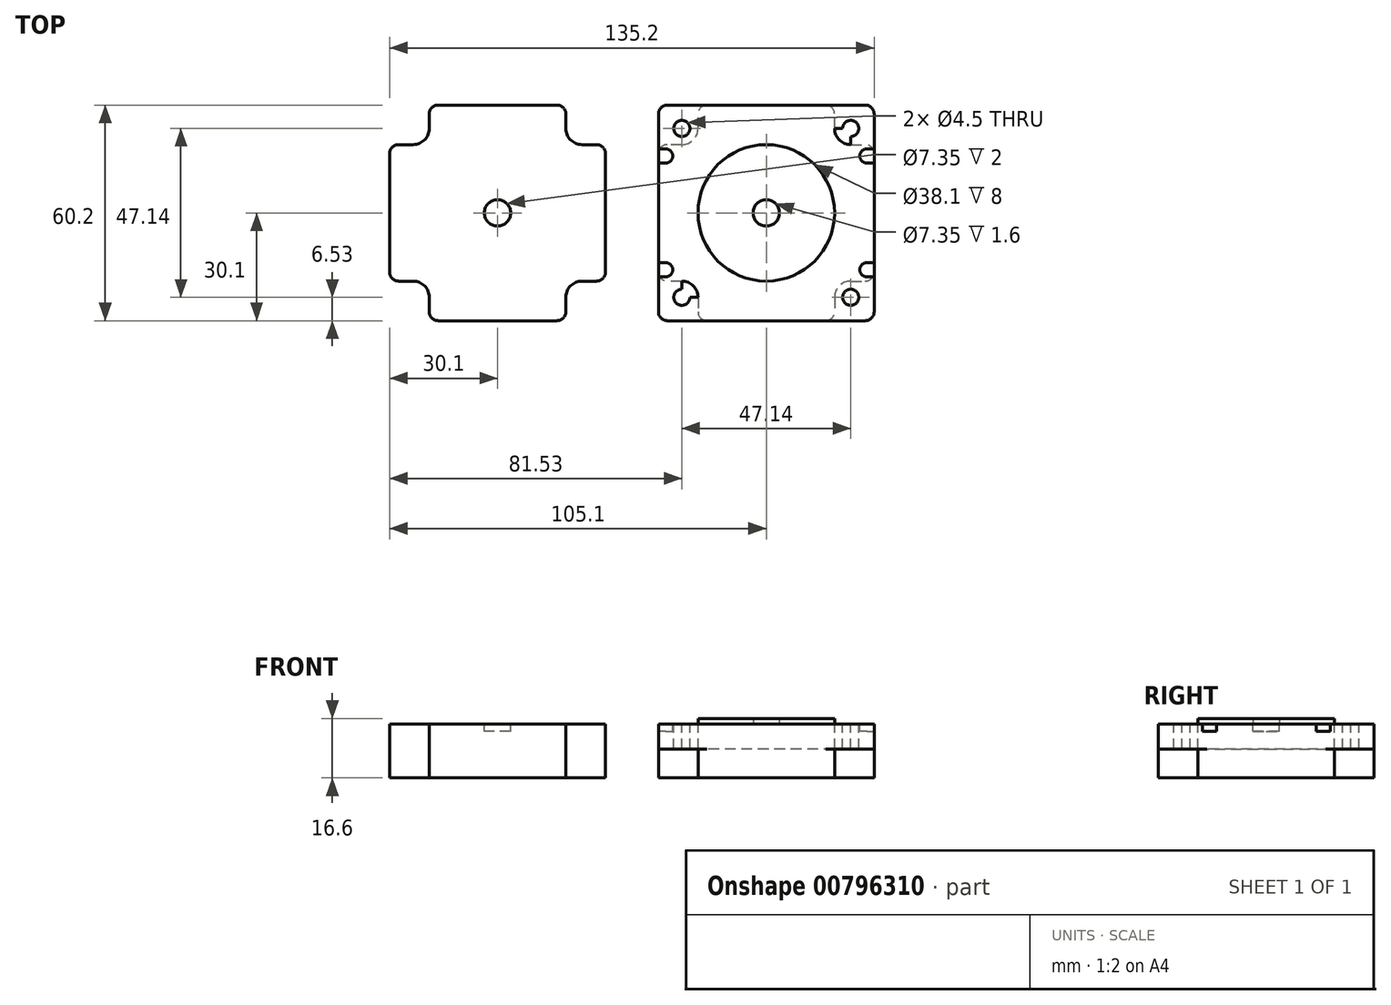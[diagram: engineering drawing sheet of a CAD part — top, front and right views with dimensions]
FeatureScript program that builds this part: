
annotation { "Feature Type Name" : "Feature", "Feature Type Description" : "" }
export const myFeature = defineFeature(function(context is Context, id is Id, definition is map)
    precondition{}
    {
        {
            var Q0;
            Q0=qCreatedBy(makeId("Top.planeOp"),FACE);
            var sketch = newSketch(context, id + "F0", { "sketchPlane" : qUnion([Q0])});
            skLineSegment(sketch, "E0.bottom", {"start": v(30.1, 30.1) * mm, "end": v(-30.1, 30.1) * mm});
            skLineSegment(sketch, "E0.top", {"start": v(30.1, -30.1) * mm, "end": v(-30.1, -30.1) * mm});
            skLineSegment(sketch, "E0.left", {"start": v(30.1, 30.1) * mm, "end": v(30.1, -30.1) * mm});
            skLineSegment(sketch, "E0.right", {"start": v(-30.1, 30.1) * mm, "end": v(-30.1, -30.1) * mm});
            skPoint(sketch, "E0.middle", {"position": v(0, 0) * mm});
            skLineSegment(sketch, "E1", {"start": v(-30.1, 30.1) * mm, "end": v(30.1, -30.1) * mm, "construction": true});
            skLineSegment(sketch, "E2", {"start": v(30.1, 30.1) * mm, "end": v(-30.1, -30.1) * mm, "construction": true});
            skLineSegment(sketch, "E3", {"start": v(-23.57, 23.57) * mm, "end": v(23.57, 23.57) * mm});
            skLineSegment(sketch, "E4", {"start": v(23.57, 23.57) * mm, "end": v(23.57, -23.57) * mm});
            skLineSegment(sketch, "E5", {"start": v(23.57, -23.57) * mm, "end": v(-23.57, -23.57) * mm});
            skLineSegment(sketch, "E6", {"start": v(-23.57, -23.57) * mm, "end": v(-23.57, 23.57) * mm});
            skCircle(sketch, "E7", {"center": v(0, 0) * mm, "radius": 19.05 * mm});
            skCircle(sketch, "E8", {"center": v(-23.57, 23.57) * mm, "radius": 2.25 * mm});
            skCircle(sketch, "E9", {"center": v(23.57, 23.57) * mm, "radius": 2.25 * mm});
            skCircle(sketch, "E10", {"center": v(23.57, -23.57) * mm, "radius": 2.25 * mm});
            skCircle(sketch, "E11", {"center": v(-23.57, -23.57) * mm, "radius": 2.25 * mm});
            skCircle(sketch, "E12", {"center": v(0, 0) * mm, "radius": 3.67 * mm});
            skLineSegment(sketch, "E13", {"start": v(0, 0) * mm, "end": v(0, -23.57) * mm, "construction": true});
            skArc(sketch, "E14", {"start": v(-28.1, -17.88) * mm, "mid": v(-26.1, -15.88) * mm, "end": v(-28.1, -13.88) * mm});
            skLineSegment(sketch, "E15", {"start": v(0, 0) * mm, "end": v(-23.57, 0) * mm, "construction": true});
            skLineSegment(sketch, "E16", {"start": v(-28.1, -13.88) * mm, "end": v(-30.1, -13.88) * mm});
            skLineSegment(sketch, "E17", {"start": v(-28.1, -17.88) * mm, "end": v(-30.1, -17.88) * mm});
            skArc(sketch, "E18", {"start": v(-28.1, -13.88) * mm, "mid": v(-30.1, -15.88) * mm, "end": v(-28.1, -17.88) * mm, "construction": true});
            skLineSegment(sketch, "E19.MirrorCS", {"start": v(-28.1, 13.88) * mm, "end": v(-30.1, 13.88) * mm});
            skArc(sketch, "E20.MirrorCS", {"start": v(-28.1, 17.88) * mm, "mid": v(-26.1, 15.88) * mm, "end": v(-28.1, 13.88) * mm});
            skLineSegment(sketch, "E21.MirrorCS", {"start": v(-28.1, 17.88) * mm, "end": v(-30.1, 17.88) * mm});
            skLineSegment(sketch, "E22.MirrorCS", {"start": v(28.1, -13.87) * mm, "end": v(30.1, -13.87) * mm});
            skArc(sketch, "E23.MirrorCS", {"start": v(28.1, -17.88) * mm, "mid": v(26.1, -15.88) * mm, "end": v(28.1, -13.88) * mm});
            skLineSegment(sketch, "E24.MirrorCS", {"start": v(28.1, -17.88) * mm, "end": v(30.1, -17.88) * mm});
            skLineSegment(sketch, "E25.MirrorCS", {"start": v(28.1, 13.88) * mm, "end": v(30.1, 13.88) * mm});
            skArc(sketch, "E26.MirrorCS", {"start": v(28.1, 17.88) * mm, "mid": v(26.1, 15.88) * mm, "end": v(28.1, 13.88) * mm});
            skLineSegment(sketch, "E27.MirrorCS", {"start": v(28.1, 17.88) * mm, "end": v(30.1, 17.88) * mm});
            skLineSegment(sketch, "E28", {"start": v(-23.57, 19.05) * mm, "end": v(-30.1, 19.05) * mm});
            skLineSegment(sketch, "E29.MirrorCS", {"start": v(-23.57, -19.05) * mm, "end": v(-30.1, -19.05) * mm});
            skLineSegment(sketch, "E30", {"start": v(-19.05, -23.57) * mm, "end": v(-19.05, -30.1) * mm});
            skLineSegment(sketch, "E31.MirrorCS", {"start": v(19.05, -23.57) * mm, "end": v(19.05, -30.1) * mm});
            skArc(sketch, "E32", {"start": v(-23.57, -19.05) * mm, "mid": v(-20.37, -20.37) * mm, "end": v(-19.05, -23.57) * mm});
            skArc(sketch, "E33.MirrorCS", {"start": v(-23.57, 19.05) * mm, "mid": v(-20.37, 20.37) * mm, "end": v(-19.05, 23.57) * mm});
            skLineSegment(sketch, "E34.MirrorCS", {"start": v(-19.05, 23.57) * mm, "end": v(-19.05, 30.1) * mm});
            skArc(sketch, "E35.MirrorCS", {"start": v(23.57, -19.05) * mm, "mid": v(20.37, -20.37) * mm, "end": v(19.05, -23.57) * mm});
            skLineSegment(sketch, "E36.MirrorCS", {"start": v(23.57, -19.05) * mm, "end": v(30.1, -19.05) * mm});
            skLineSegment(sketch, "E37.MirrorCS", {"start": v(23.57, 19.05) * mm, "end": v(30.1, 19.05) * mm});
            skArc(sketch, "E38.MirrorCS", {"start": v(23.57, 19.05) * mm, "mid": v(20.37, 20.37) * mm, "end": v(19.05, 23.57) * mm});
            skLineSegment(sketch, "E39.MirrorCS", {"start": v(19.05, 23.57) * mm, "end": v(19.05, 30.1) * mm});
            skLineSegment(sketch, "E40.1.0.0", {"start": v(-75, 0) * mm, "end": v(-75, -23.57) * mm, "construction": true});
            skLineSegment(sketch, "E40.1.0.1", {"start": v(-55.95, -23.57) * mm, "end": v(-55.95, -30.1) * mm});
            skArc(sketch, "E40.1.0.2", {"start": v(-51.43, -19.05) * mm, "mid": v(-54.63, -20.37) * mm, "end": v(-55.95, -23.57) * mm});
            skLineSegment(sketch, "E40.1.0.3", {"start": v(-51.43, -19.05) * mm, "end": v(-44.9, -19.05) * mm});
            skLineSegment(sketch, "E40.1.0.4", {"start": v(-44.9, 30.1) * mm, "end": v(-44.9, -30.1) * mm});
            skLineSegment(sketch, "E40.1.0.5", {"start": v(-51.43, 19.05) * mm, "end": v(-44.9, 19.05) * mm});
            skArc(sketch, "E40.1.0.6", {"start": v(-51.43, 19.05) * mm, "mid": v(-54.63, 20.37) * mm, "end": v(-55.95, 23.57) * mm});
            skLineSegment(sketch, "E40.1.0.7", {"start": v(-55.95, 23.57) * mm, "end": v(-55.95, 30.1) * mm});
            skLineSegment(sketch, "E40.1.0.8", {"start": v(-44.9, 30.1) * mm, "end": v(-105.1, 30.1) * mm});
            skLineSegment(sketch, "E40.1.0.9", {"start": v(-94.05, 23.57) * mm, "end": v(-94.05, 30.1) * mm});
            skArc(sketch, "E40.1.0.10", {"start": v(-98.57, 19.05) * mm, "mid": v(-95.37, 20.37) * mm, "end": v(-94.05, 23.57) * mm});
            skLineSegment(sketch, "E40.1.0.11", {"start": v(-98.57, 19.05) * mm, "end": v(-105.1, 19.05) * mm});
            skLineSegment(sketch, "E40.1.0.12", {"start": v(-105.1, 30.1) * mm, "end": v(-105.1, -30.1) * mm});
            skLineSegment(sketch, "E40.1.0.13", {"start": v(-98.57, -19.05) * mm, "end": v(-105.1, -19.05) * mm});
            skArc(sketch, "E40.1.0.14", {"start": v(-98.57, -19.05) * mm, "mid": v(-95.37, -20.37) * mm, "end": v(-94.05, -23.57) * mm});
            skLineSegment(sketch, "E40.1.0.15", {"start": v(-94.05, -23.57) * mm, "end": v(-94.05, -30.1) * mm});
            skLineSegment(sketch, "E40.1.0.16", {"start": v(-44.9, -30.1) * mm, "end": v(-105.1, -30.1) * mm});
            skCircle(sketch, "E40.1.0.17", {"center": v(-75, 0) * mm, "radius": 3.67 * mm});
            skLineSegment(sketch, "E40.2.0.0", {"start": v(-150, 0) * mm, "end": v(-150, -23.57) * mm, "construction": true});
            skLineSegment(sketch, "E40.2.0.1", {"start": v(-130.95, -23.57) * mm, "end": v(-130.95, -30.1) * mm});
            skArc(sketch, "E40.2.0.2", {"start": v(-126.43, -19.05) * mm, "mid": v(-129.63, -20.37) * mm, "end": v(-130.95, -23.57) * mm});
            skLineSegment(sketch, "E40.2.0.3", {"start": v(-126.43, -19.05) * mm, "end": v(-119.9, -19.05) * mm});
            skLineSegment(sketch, "E40.2.0.4", {"start": v(-119.9, 30.1) * mm, "end": v(-119.9, -30.1) * mm});
            skLineSegment(sketch, "E40.2.0.5", {"start": v(-126.43, 19.05) * mm, "end": v(-119.9, 19.05) * mm});
            skArc(sketch, "E40.2.0.6", {"start": v(-126.43, 19.05) * mm, "mid": v(-129.63, 20.37) * mm, "end": v(-130.95, 23.57) * mm});
            skLineSegment(sketch, "E40.2.0.7", {"start": v(-130.95, 23.57) * mm, "end": v(-130.95, 30.1) * mm});
            skLineSegment(sketch, "E40.2.0.8", {"start": v(-119.9, 30.1) * mm, "end": v(-180.1, 30.1) * mm});
            skLineSegment(sketch, "E40.2.0.9", {"start": v(-169.05, 23.57) * mm, "end": v(-169.05, 30.1) * mm});
            skArc(sketch, "E40.2.0.10", {"start": v(-173.57, 19.05) * mm, "mid": v(-170.37, 20.37) * mm, "end": v(-169.05, 23.57) * mm});
            skLineSegment(sketch, "E40.2.0.11", {"start": v(-173.57, 19.05) * mm, "end": v(-180.1, 19.05) * mm});
            skLineSegment(sketch, "E40.2.0.12", {"start": v(-180.1, 30.1) * mm, "end": v(-180.1, -30.1) * mm});
            skLineSegment(sketch, "E40.2.0.13", {"start": v(-173.57, -19.05) * mm, "end": v(-180.1, -19.05) * mm});
            skArc(sketch, "E40.2.0.14", {"start": v(-173.57, -19.05) * mm, "mid": v(-170.37, -20.37) * mm, "end": v(-169.05, -23.57) * mm});
            skLineSegment(sketch, "E40.2.0.15", {"start": v(-169.05, -23.57) * mm, "end": v(-169.05, -30.1) * mm});
            skLineSegment(sketch, "E40.2.0.16", {"start": v(-119.9, -30.1) * mm, "end": v(-180.1, -30.1) * mm});
            skCircle(sketch, "E40.2.0.17", {"center": v(-150, 0) * mm, "radius": 3.67 * mm});
            skLineSegment(sketch, "E40.direction1", {"start": v(0, -23.57) * mm, "end": v(-75, -23.57) * mm, "construction": true});
            skLineSegment(sketch, "E41.0.3.0", {"start": v(-225, 0) * mm, "end": v(-225, -23.57) * mm, "construction": true});
            skLineSegment(sketch, "E41.3.3.0", {"start": v(-205.95, -23.57) * mm, "end": v(-205.95, -30.1) * mm});
            skArc(sketch, "E41.6.3.0", {"start": v(-201.43, -19.05) * mm, "mid": v(-204.63, -20.37) * mm, "end": v(-205.95, -23.57) * mm});
            skLineSegment(sketch, "E41.10.3.0", {"start": v(-201.43, -19.05) * mm, "end": v(-194.9, -19.05) * mm});
            skLineSegment(sketch, "E41.13.3.0", {"start": v(-194.9, 30.1) * mm, "end": v(-194.9, -30.1) * mm});
            skLineSegment(sketch, "E41.16.3.0", {"start": v(-201.43, 19.05) * mm, "end": v(-194.9, 19.05) * mm});
            skArc(sketch, "E41.19.3.0", {"start": v(-201.43, 19.05) * mm, "mid": v(-204.63, 20.37) * mm, "end": v(-205.95, 23.57) * mm});
            skLineSegment(sketch, "E41.23.3.0", {"start": v(-205.95, 23.57) * mm, "end": v(-205.95, 30.1) * mm});
            skLineSegment(sketch, "E41.26.3.0", {"start": v(-194.9, 30.1) * mm, "end": v(-255.1, 30.1) * mm});
            skLineSegment(sketch, "E41.29.3.0", {"start": v(-244.05, 23.57) * mm, "end": v(-244.05, 30.1) * mm});
            skArc(sketch, "E41.32.3.0", {"start": v(-248.57, 19.05) * mm, "mid": v(-245.37, 20.37) * mm, "end": v(-244.05, 23.57) * mm});
            skLineSegment(sketch, "E41.36.3.0", {"start": v(-248.57, 19.05) * mm, "end": v(-255.1, 19.05) * mm});
            skLineSegment(sketch, "E41.39.3.0", {"start": v(-255.1, 30.1) * mm, "end": v(-255.1, -30.1) * mm});
            skLineSegment(sketch, "E41.42.3.0", {"start": v(-248.57, -19.05) * mm, "end": v(-255.1, -19.05) * mm});
            skArc(sketch, "E41.45.3.0", {"start": v(-248.57, -19.05) * mm, "mid": v(-245.37, -20.37) * mm, "end": v(-244.05, -23.57) * mm});
            skLineSegment(sketch, "E41.49.3.0", {"start": v(-244.05, -23.57) * mm, "end": v(-244.05, -30.1) * mm});
            skLineSegment(sketch, "E41.52.3.0", {"start": v(-194.9, -30.1) * mm, "end": v(-255.1, -30.1) * mm});
            skCircle(sketch, "E41.55.3.0", {"center": v(-225, 0) * mm, "radius": 3.67 * mm});
            skLineSegment(sketch, "E41.0.4.0", {"start": v(-300, 0) * mm, "end": v(-300, -23.57) * mm, "construction": true});
            skLineSegment(sketch, "E41.3.4.0", {"start": v(-280.95, -23.57) * mm, "end": v(-280.95, -30.1) * mm});
            skArc(sketch, "E41.6.4.0", {"start": v(-276.43, -19.05) * mm, "mid": v(-279.63, -20.37) * mm, "end": v(-280.95, -23.57) * mm});
            skLineSegment(sketch, "E41.10.4.0", {"start": v(-276.43, -19.05) * mm, "end": v(-269.9, -19.05) * mm});
            skLineSegment(sketch, "E41.13.4.0", {"start": v(-269.9, 30.1) * mm, "end": v(-269.9, -30.1) * mm});
            skLineSegment(sketch, "E41.16.4.0", {"start": v(-276.43, 19.05) * mm, "end": v(-269.9, 19.05) * mm});
            skArc(sketch, "E41.19.4.0", {"start": v(-276.43, 19.05) * mm, "mid": v(-279.63, 20.37) * mm, "end": v(-280.95, 23.57) * mm});
            skLineSegment(sketch, "E41.23.4.0", {"start": v(-280.95, 23.57) * mm, "end": v(-280.95, 30.1) * mm});
            skLineSegment(sketch, "E41.26.4.0", {"start": v(-269.9, 30.1) * mm, "end": v(-330.1, 30.1) * mm});
            skLineSegment(sketch, "E41.29.4.0", {"start": v(-319.05, 23.57) * mm, "end": v(-319.05, 30.1) * mm});
            skArc(sketch, "E41.32.4.0", {"start": v(-323.57, 19.05) * mm, "mid": v(-320.37, 20.37) * mm, "end": v(-319.05, 23.57) * mm});
            skLineSegment(sketch, "E41.36.4.0", {"start": v(-323.57, 19.05) * mm, "end": v(-330.1, 19.05) * mm});
            skLineSegment(sketch, "E41.39.4.0", {"start": v(-330.1, 30.1) * mm, "end": v(-330.1, -30.1) * mm});
            skLineSegment(sketch, "E41.42.4.0", {"start": v(-323.57, -19.05) * mm, "end": v(-330.1, -19.05) * mm});
            skArc(sketch, "E41.45.4.0", {"start": v(-323.57, -19.05) * mm, "mid": v(-320.37, -20.37) * mm, "end": v(-319.05, -23.57) * mm});
            skLineSegment(sketch, "E41.49.4.0", {"start": v(-319.05, -23.57) * mm, "end": v(-319.05, -30.1) * mm});
            skLineSegment(sketch, "E41.52.4.0", {"start": v(-269.9, -30.1) * mm, "end": v(-330.1, -30.1) * mm});
            skCircle(sketch, "E41.55.4.0", {"center": v(-300, 0) * mm, "radius": 3.67 * mm});
            skLineSegment(sketch, "E42.0.5.0", {"start": v(-375, 0) * mm, "end": v(-375, -23.57) * mm, "construction": true});
            skLineSegment(sketch, "E42.3.5.0", {"start": v(-355.95, -23.57) * mm, "end": v(-355.95, -30.1) * mm});
            skArc(sketch, "E42.6.5.0", {"start": v(-351.43, -19.05) * mm, "mid": v(-354.63, -20.37) * mm, "end": v(-355.95, -23.57) * mm});
            skLineSegment(sketch, "E42.10.5.0", {"start": v(-351.43, -19.05) * mm, "end": v(-344.9, -19.05) * mm});
            skLineSegment(sketch, "E42.13.5.0", {"start": v(-344.9, 30.1) * mm, "end": v(-344.9, -30.1) * mm});
            skLineSegment(sketch, "E42.16.5.0", {"start": v(-351.43, 19.05) * mm, "end": v(-344.9, 19.05) * mm});
            skArc(sketch, "E42.19.5.0", {"start": v(-351.43, 19.05) * mm, "mid": v(-354.63, 20.37) * mm, "end": v(-355.95, 23.57) * mm});
            skLineSegment(sketch, "E42.23.5.0", {"start": v(-355.95, 23.57) * mm, "end": v(-355.95, 30.1) * mm});
            skLineSegment(sketch, "E42.26.5.0", {"start": v(-344.9, 30.1) * mm, "end": v(-405.1, 30.1) * mm});
            skLineSegment(sketch, "E42.29.5.0", {"start": v(-394.05, 23.57) * mm, "end": v(-394.05, 30.1) * mm});
            skArc(sketch, "E42.32.5.0", {"start": v(-398.57, 19.05) * mm, "mid": v(-395.37, 20.37) * mm, "end": v(-394.05, 23.57) * mm});
            skLineSegment(sketch, "E42.36.5.0", {"start": v(-398.57, 19.05) * mm, "end": v(-405.1, 19.05) * mm});
            skLineSegment(sketch, "E42.39.5.0", {"start": v(-405.1, 30.1) * mm, "end": v(-405.1, -30.1) * mm});
            skLineSegment(sketch, "E42.42.5.0", {"start": v(-398.57, -19.05) * mm, "end": v(-405.1, -19.05) * mm});
            skArc(sketch, "E42.45.5.0", {"start": v(-398.57, -19.05) * mm, "mid": v(-395.37, -20.37) * mm, "end": v(-394.05, -23.57) * mm});
            skLineSegment(sketch, "E42.49.5.0", {"start": v(-394.05, -23.57) * mm, "end": v(-394.05, -30.1) * mm});
            skLineSegment(sketch, "E42.52.5.0", {"start": v(-344.9, -30.1) * mm, "end": v(-405.1, -30.1) * mm});
            skCircle(sketch, "E42.55.5.0", {"center": v(-375, 0) * mm, "radius": 3.67 * mm});
            skSolve(sketch);
        }
        {
            var Q0;
            Q0=makeQuery(id+"F0.imprint","IMPRINT",FACE,{"disambiguationData":[TD([[makeQuery(id+"F0.imprint","IMPRINT",EDGE,{"derivedFrom":sQuery(id+"F0.wireOp",EDGE,"E14")}),-1.0]])]});
            var Q1;
            {var subQ0=sQuery(id+"F0.wireOp",EDGE,"E19.MirrorCS");Q1=makeQuery(id+"F0.imprint","IMPRINT",FACE,{"disambiguationData":[TD([[makeQuery(id+"F0.imprint","IMPRINT",EDGE,{"derivedFrom":subQ0}),-1.0]])]});}
            var Q2;
            Q2=makeQuery(id+"F0.imprint","IMPRINT",FACE,{"disambiguationData":[TD([[makeQuery(id+"F0.imprint","IMPRINT",EDGE,{"derivedFrom":sQuery(id+"F0.wireOp",EDGE,"E14")}),1.0]])]});
            var Q3;
            {var subQ5=sQuery(id+"F0.wireOp",EDGE,"E28");Q3=makeQuery(id+"F0.imprint","IMPRINT",FACE,{"disambiguationData":[TD([[makeQuery(id+"F0.imprint","IMPRINT",EDGE,{"derivedFrom":subQ5}),-1.0]])]});}
            var Q4;
            {var subQ0=sQuery(id+"F0.wireOp",EDGE,"E33.MirrorCS");Q4=makeQuery(id+"F0.imprint","IMPRINT",FACE,{"disambiguationData":[TD([[makeQuery(id+"F0.imprint","IMPRINT",EDGE,{"derivedFrom":subQ0}),1.0]])]});}
            var Q5;
            {var subQ0=sQuery(id+"F0.wireOp",EDGE,"E34.MirrorCS");Q5=makeQuery(id+"F0.imprint","IMPRINT",FACE,{"disambiguationData":[TD([[makeQuery(id+"F0.imprint","IMPRINT",EDGE,{"derivedFrom":subQ0}),-1.0]])]});}
            var Q6;
            {var subQ5=sQuery(id+"F0.wireOp",EDGE,"E37.MirrorCS");Q6=makeQuery(id+"F0.imprint","IMPRINT",FACE,{"disambiguationData":[TD([[makeQuery(id+"F0.imprint","IMPRINT",EDGE,{"derivedFrom":subQ5}),1.0]])]});}
            var Q7;
            Q7=makeQuery(id+"F0.imprint","IMPRINT",FACE,{"disambiguationData":[TD([[makeQuery(id+"F0.imprint","IMPRINT",EDGE,{"derivedFrom":sQuery(id+"F0.wireOp",EDGE,"E12")}),1.0]])]});
            var Q8;
            Q8=makeQuery(id+"F0.imprint","IMPRINT",FACE,{"disambiguationData":[TD([[makeQuery(id+"F0.imprint","IMPRINT",EDGE,{"derivedFrom":sQuery(id+"F0.wireOp",EDGE,"E7")}),-1.0]])]});
            var Q9;
            {var subQ0=sQuery(id+"F0.wireOp",EDGE,"E22.MirrorCS");Q9=makeQuery(id+"F0.imprint","IMPRINT",FACE,{"disambiguationData":[TD([[makeQuery(id+"F0.imprint","IMPRINT",EDGE,{"derivedFrom":subQ0}),-1.0]])]});}
            var Q10;
            {var subQ0=sQuery(id+"F0.wireOp",EDGE,"E32");Q10=makeQuery(id+"F0.imprint","IMPRINT",FACE,{"disambiguationData":[TD([[makeQuery(id+"F0.imprint","IMPRINT",EDGE,{"derivedFrom":subQ0}),-1.0]])]});}
            var Q11;
            {var subQ5=sQuery(id+"F0.wireOp",EDGE,"E22.MirrorCS");Q11=makeQuery(id+"F0.imprint","IMPRINT",FACE,{"disambiguationData":[TD([[makeQuery(id+"F0.imprint","IMPRINT",EDGE,{"derivedFrom":subQ5}),1.0]])]});}
            var Q12;
            {var subQ1=sQuery(id+"F0.wireOp",EDGE,"E29.MirrorCS");Q12=makeQuery(id+"F0.imprint","IMPRINT",FACE,{"disambiguationData":[TD([[makeQuery(id+"F0.imprint","IMPRINT",EDGE,{"derivedFrom":subQ1}),1.0]])]});}
            var Q13;
            {var subQ0=sQuery(id+"F0.wireOp",EDGE,"E35.MirrorCS");Q13=makeQuery(id+"F0.imprint","IMPRINT",FACE,{"disambiguationData":[TD([[makeQuery(id+"F0.imprint","IMPRINT",EDGE,{"derivedFrom":subQ0}),1.0]])]});}
            var Q14;
            {var subQ0=sQuery(id+"F0.wireOp",EDGE,"E30");Q14=makeQuery(id+"F0.imprint","IMPRINT",FACE,{"disambiguationData":[TD([[makeQuery(id+"F0.imprint","IMPRINT",EDGE,{"derivedFrom":subQ0}),1.0]])]});}
            var Q15;
            {var subQ1=sQuery(id+"F0.wireOp",EDGE,"E31.MirrorCS");Q15=makeQuery(id+"F0.imprint","IMPRINT",FACE,{"disambiguationData":[TD([[makeQuery(id+"F0.imprint","IMPRINT",EDGE,{"derivedFrom":subQ1}),1.0]])]});}
            var Q16;
            {var subQ0=sQuery(id+"F0.wireOp",EDGE,"E25.MirrorCS");Q16=makeQuery(id+"F0.imprint","IMPRINT",FACE,{"disambiguationData":[TD([[makeQuery(id+"F0.imprint","IMPRINT",EDGE,{"derivedFrom":subQ0}),1.0]])]});}
            var Q17;
            Q17=makeQuery(id+"F0.imprint","IMPRINT",FACE,{"disambiguationData":[TD([[makeQuery(id+"F0.imprint","IMPRINT",EDGE,{"derivedFrom":sQuery(id+"F0.wireOp",EDGE,"E7")}),1.0]])]});
            var Q18;
            {var subQ0=sQuery(id+"F0.wireOp",EDGE,"E38.MirrorCS");Q18=makeQuery(id+"F0.imprint","IMPRINT",FACE,{"disambiguationData":[TD([[makeQuery(id+"F0.imprint","IMPRINT",EDGE,{"derivedFrom":subQ0}),-1.0]])]});}
            extrude(context, id + "F1", {"entities" : qUnion([Q0, Q1, Q2, Q3, Q4, Q5, Q6, Q7, Q8, Q9, Q10, Q11, Q12, Q13, Q14, Q15, Q16, Q17, Q18]), "oppositeDirection" : true, "depth" : 7 * mm, "offsetDistance" : 25 * mm});
        }
        {
            var Q0;
            Q0=makeQuery(id+"F0.imprint","IMPRINT",FACE,{"disambiguationData":[TD([[makeQuery(id+"F0.imprint","IMPRINT",EDGE,{"derivedFrom":sQuery(id+"F0.wireOp",EDGE,"E14")}),-1.0]])]});
            var Q1;
            {var subQ0=sQuery(id+"F0.wireOp",EDGE,"E19.MirrorCS");Q1=makeQuery(id+"F0.imprint","IMPRINT",FACE,{"disambiguationData":[TD([[makeQuery(id+"F0.imprint","IMPRINT",EDGE,{"derivedFrom":subQ0}),-1.0]])]});}
            var Q2;
            Q2=makeQuery(id+"F0.imprint","IMPRINT",FACE,{"disambiguationData":[TD([[makeQuery(id+"F0.imprint","IMPRINT",EDGE,{"derivedFrom":sQuery(id+"F0.wireOp",EDGE,"E14")}),1.0]])]});
            var Q3;
            Q3=makeQuery(id+"F0.imprint","IMPRINT",FACE,{"disambiguationData":[TD([[makeQuery(id+"F0.imprint","IMPRINT",EDGE,{"derivedFrom":sQuery(id+"F0.wireOp",EDGE,"E7")}),-1.0]])]});
            var Q4;
            {var subQ0=sQuery(id+"F0.wireOp",EDGE,"E30");Q4=makeQuery(id+"F0.imprint","IMPRINT",FACE,{"disambiguationData":[TD([[makeQuery(id+"F0.imprint","IMPRINT",EDGE,{"derivedFrom":subQ0}),1.0]])]});}
            var Q5;
            {var subQ5=sQuery(id+"F0.wireOp",EDGE,"E22.MirrorCS");Q5=makeQuery(id+"F0.imprint","IMPRINT",FACE,{"disambiguationData":[TD([[makeQuery(id+"F0.imprint","IMPRINT",EDGE,{"derivedFrom":subQ5}),1.0]])]});}
            var Q6;
            {var subQ0=sQuery(id+"F0.wireOp",EDGE,"E22.MirrorCS");Q6=makeQuery(id+"F0.imprint","IMPRINT",FACE,{"disambiguationData":[TD([[makeQuery(id+"F0.imprint","IMPRINT",EDGE,{"derivedFrom":subQ0}),-1.0]])]});}
            var Q7;
            {var subQ0=sQuery(id+"F0.wireOp",EDGE,"E25.MirrorCS");Q7=makeQuery(id+"F0.imprint","IMPRINT",FACE,{"disambiguationData":[TD([[makeQuery(id+"F0.imprint","IMPRINT",EDGE,{"derivedFrom":subQ0}),1.0]])]});}
            var Q8;
            {var subQ0=sQuery(id+"F0.wireOp",EDGE,"E34.MirrorCS");Q8=makeQuery(id+"F0.imprint","IMPRINT",FACE,{"disambiguationData":[TD([[makeQuery(id+"F0.imprint","IMPRINT",EDGE,{"derivedFrom":subQ0}),-1.0]])]});}
            extrude(context, id + "F2", {"entities" : qUnion([Q0, Q1, Q2, Q3, Q4, Q5, Q6, Q7, Q8]), "operationType" : NewBodyOperationType.ADD, "oppositeDirection" : true, "depth" : 15 * mm, "offsetDistance" : 25 * mm});
        }
        {
            var Q0;
            Q0=makeQuery(id+"F0.imprint","IMPRINT",FACE,{"disambiguationData":[TD([[makeQuery(id+"F0.imprint","IMPRINT",EDGE,{"derivedFrom":sQuery(id+"F0.wireOp",EDGE,"E7")}),1.0]])]});
            extrude(context, id + "F3", {"entities" : qUnion([Q0]), "operationType" : NewBodyOperationType.ADD, "depth" : 1.6 * mm, "offsetDistance" : 25 * mm});
        }
        {
            var Q0;
            {var subQ0=sQuery(id+"F0.wireOp",EDGE,"E19.MirrorCS");Q0=makeQuery(id+"F0.imprint","IMPRINT",FACE,{"disambiguationData":[TD([[makeQuery(id+"F0.imprint","IMPRINT",EDGE,{"derivedFrom":subQ0}),-1.0]])]});}
            var Q1;
            Q1=makeQuery(id+"F0.imprint","IMPRINT",FACE,{"disambiguationData":[TD([[makeQuery(id+"F0.imprint","IMPRINT",EDGE,{"derivedFrom":sQuery(id+"F0.wireOp",EDGE,"E14")}),1.0]])]});
            var Q2;
            {var subQ0=sQuery(id+"F0.wireOp",EDGE,"E25.MirrorCS");Q2=makeQuery(id+"F0.imprint","IMPRINT",FACE,{"disambiguationData":[TD([[makeQuery(id+"F0.imprint","IMPRINT",EDGE,{"derivedFrom":subQ0}),1.0]])]});}
            var Q3;
            {var subQ0=sQuery(id+"F0.wireOp",EDGE,"E22.MirrorCS");Q3=makeQuery(id+"F0.imprint","IMPRINT",FACE,{"disambiguationData":[TD([[makeQuery(id+"F0.imprint","IMPRINT",EDGE,{"derivedFrom":subQ0}),-1.0]])]});}
            extrude(context, id + "F4", {"entities" : qUnion([Q0, Q1, Q2, Q3]), "operationType" : NewBodyOperationType.REMOVE, "oppositeDirection" : true, "depth" : 2 * mm, "offsetDistance" : 25 * mm});
        }
        {
            var Q0;
            {var subQ4=sQuery(id+"F0.wireOp",EDGE,"E40.1.0.1");Q0=makeQuery(id+"F0.imprint","IMPRINT",FACE,{"disambiguationData":[TD([[makeQuery(id+"F0.imprint","IMPRINT",EDGE,{"derivedFrom":subQ4}),-1.0]])]});}
            var Q1;
            Q1=makeQuery(id+"F0.imprint","IMPRINT",FACE,{"disambiguationData":[TD([[makeQuery(id+"F0.imprint","IMPRINT",EDGE,{"derivedFrom":sQuery(id+"F0.wireOp",EDGE,"E40.1.0.17")}),1.0]])]});
            extrude(context, id + "F5", {"entities" : qUnion([Q0, Q1]), "oppositeDirection" : true, "depth" : 15 * mm, "offsetDistance" : 25 * mm});
        }
        {
            var Q0;
            Q0=makeQuery(id+"F0.imprint","IMPRINT",FACE,{"disambiguationData":[TD([[makeQuery(id+"F0.imprint","IMPRINT",EDGE,{"derivedFrom":sQuery(id+"F0.wireOp",EDGE,"E40.1.0.17")}),1.0]])]});
            extrude(context, id + "F6", {"entities" : qUnion([Q0]), "operationType" : NewBodyOperationType.REMOVE, "oppositeDirection" : true, "depth" : 2 * mm, "offsetDistance" : 25 * mm});
        }
        {
            var Q0;
            Q0=makeQuery(id+"F1.opExtrude","SWEPT_EDGE",EDGE,{"disambiguationData":[OSD([sQuery(id+"F0.wireOp",EDGE,"E0.top"),sQuery(id+"F0.wireOp",EDGE,"E0.right")])]});
            var Q1;
            Q1=makeQuery(id+"F2.opExtrude","SWEPT_EDGE",EDGE,{"disambiguationData":[OSD([sQuery(id+"F0.wireOp",EDGE,"E0.top"),sQuery(id+"F0.wireOp",EDGE,"E30")])]});
            var Q2;
            Q2=makeQuery(id+"F2.opExtrude","SWEPT_EDGE",EDGE,{"disambiguationData":[OSD([sQuery(id+"F0.wireOp",EDGE,"E0.right"),sQuery(id+"F0.wireOp",EDGE,"E29.MirrorCS")])]});
            var Q3;
            Q3=makeQuery(id+"F2.opExtrude","SWEPT_EDGE",EDGE,{"disambiguationData":[OSD([sQuery(id+"F0.wireOp",EDGE,"E0.top"),sQuery(id+"F0.wireOp",EDGE,"E31.MirrorCS")])]});
            var Q4;
            Q4=makeQuery(id+"F1.opExtrude","SWEPT_EDGE",EDGE,{"disambiguationData":[OSD([sQuery(id+"F0.wireOp",EDGE,"E0.top"),sQuery(id+"F0.wireOp",EDGE,"E0.left")])]});
            var Q5;
            Q5=makeQuery(id+"F2.opExtrude","SWEPT_EDGE",EDGE,{"disambiguationData":[OSD([sQuery(id+"F0.wireOp",EDGE,"E0.left"),sQuery(id+"F0.wireOp",EDGE,"E36.MirrorCS")])]});
            var Q6;
            Q6=makeQuery(id+"F2.opExtrude","SWEPT_EDGE",EDGE,{"disambiguationData":[OSD([sQuery(id+"F0.wireOp",EDGE,"E0.left"),sQuery(id+"F0.wireOp",EDGE,"E37.MirrorCS")])]});
            var Q7;
            Q7=makeQuery(id+"F1.opExtrude","SWEPT_EDGE",EDGE,{"disambiguationData":[OSD([sQuery(id+"F0.wireOp",EDGE,"E0.bottom"),sQuery(id+"F0.wireOp",EDGE,"E0.left")])]});
            var Q8;
            Q8=makeQuery(id+"F2.opExtrude","SWEPT_EDGE",EDGE,{"disambiguationData":[OSD([sQuery(id+"F0.wireOp",EDGE,"E0.bottom"),sQuery(id+"F0.wireOp",EDGE,"E39.MirrorCS")])]});
            var Q9;
            Q9=makeQuery(id+"F2.opExtrude","SWEPT_EDGE",EDGE,{"disambiguationData":[OSD([sQuery(id+"F0.wireOp",EDGE,"E0.bottom"),sQuery(id+"F0.wireOp",EDGE,"E34.MirrorCS")])]});
            var Q10;
            Q10=makeQuery(id+"F1.opExtrude","SWEPT_EDGE",EDGE,{"disambiguationData":[OSD([sQuery(id+"F0.wireOp",EDGE,"E0.bottom"),sQuery(id+"F0.wireOp",EDGE,"E0.right")])]});
            var Q11;
            Q11=makeQuery(id+"F2.opExtrude","SWEPT_EDGE",EDGE,{"disambiguationData":[OSD([sQuery(id+"F0.wireOp",EDGE,"E0.right"),sQuery(id+"F0.wireOp",EDGE,"E28")])]});
            var Q12;
            Q12=makeQuery(id+"F5.opExtrude","SWEPT_EDGE",EDGE,{"disambiguationData":[OSD([sQuery(id+"F0.wireOp",EDGE,"E40.1.0.15"),sQuery(id+"F0.wireOp",EDGE,"E40.1.0.16")])]});
            var Q13;
            Q13=makeQuery(id+"F5.opExtrude","SWEPT_EDGE",EDGE,{"disambiguationData":[OSD([sQuery(id+"F0.wireOp",EDGE,"E40.1.0.1"),sQuery(id+"F0.wireOp",EDGE,"E40.1.0.16")])]});
            var Q14;
            Q14=makeQuery(id+"F5.opExtrude","SWEPT_EDGE",EDGE,{"disambiguationData":[OSD([sQuery(id+"F0.wireOp",EDGE,"E40.1.0.3"),sQuery(id+"F0.wireOp",EDGE,"E40.1.0.4")])]});
            var Q15;
            Q15=makeQuery(id+"F5.opExtrude","SWEPT_EDGE",EDGE,{"disambiguationData":[OSD([sQuery(id+"F0.wireOp",EDGE,"E40.1.0.4"),sQuery(id+"F0.wireOp",EDGE,"E40.1.0.5")])]});
            var Q16;
            Q16=makeQuery(id+"F5.opExtrude","SWEPT_EDGE",EDGE,{"disambiguationData":[OSD([sQuery(id+"F0.wireOp",EDGE,"E40.1.0.7"),sQuery(id+"F0.wireOp",EDGE,"E40.1.0.8")])]});
            var Q17;
            Q17=makeQuery(id+"F5.opExtrude","SWEPT_EDGE",EDGE,{"disambiguationData":[OSD([sQuery(id+"F0.wireOp",EDGE,"E40.1.0.8"),sQuery(id+"F0.wireOp",EDGE,"E40.1.0.9")])]});
            var Q18;
            Q18=makeQuery(id+"F5.opExtrude","SWEPT_EDGE",EDGE,{"disambiguationData":[OSD([sQuery(id+"F0.wireOp",EDGE,"E40.1.0.11"),sQuery(id+"F0.wireOp",EDGE,"E40.1.0.12")])]});
            var Q19;
            Q19=makeQuery(id+"F5.opExtrude","SWEPT_EDGE",EDGE,{"disambiguationData":[OSD([sQuery(id+"F0.wireOp",EDGE,"E40.1.0.12"),sQuery(id+"F0.wireOp",EDGE,"E40.1.0.13")])]});
            fillet(context, id + "F7", {"entities" : qUnion([Q0, Q1, Q2, Q3, Q4, Q5, Q6, Q7, Q8, Q9, Q10, Q11, Q12, Q13, Q14, Q15, Q16, Q17, Q18, Q19]), "radius" : 2.5 * mm, "tangentPropagation" : true, "allowEdgeOverflow" : false});
        }
    });
